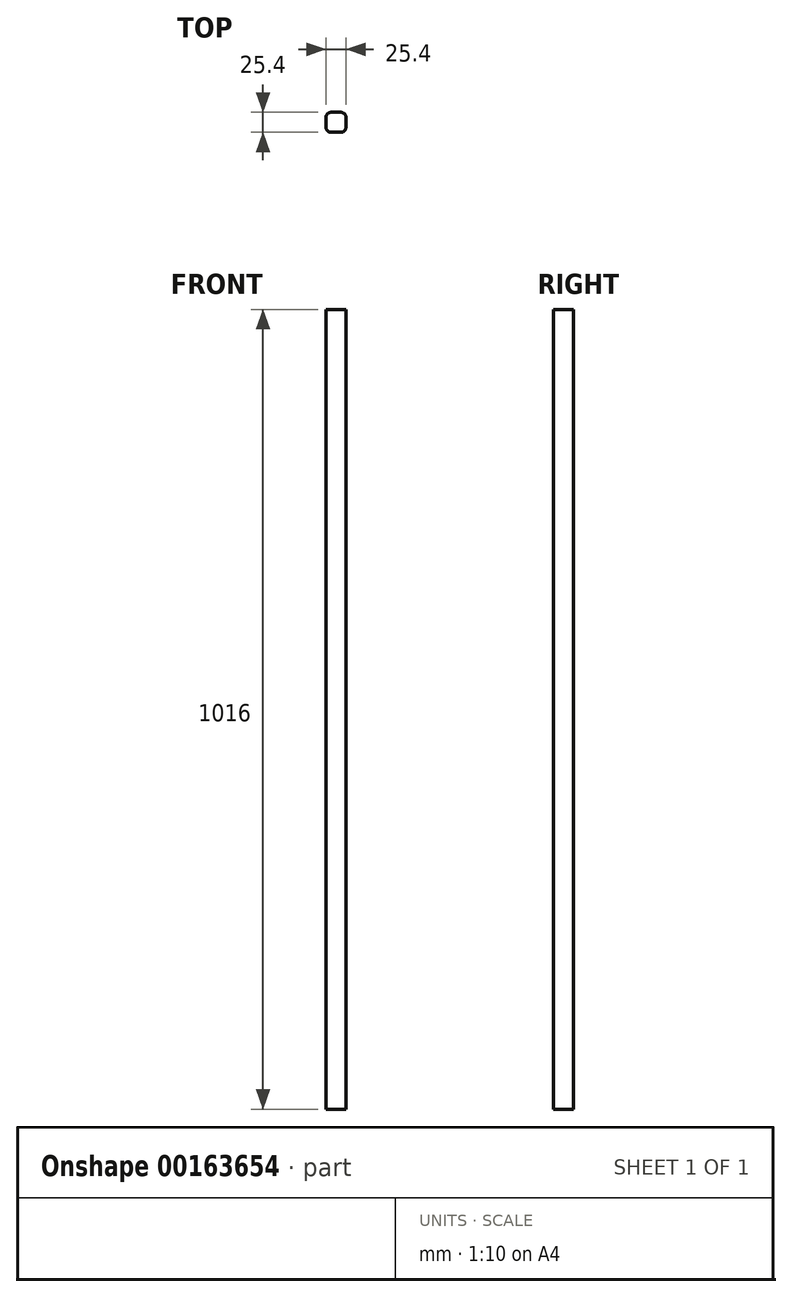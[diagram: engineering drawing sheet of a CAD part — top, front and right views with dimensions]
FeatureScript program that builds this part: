
annotation { "Feature Type Name" : "Feature", "Feature Type Description" : "" }
export const myFeature = defineFeature(function(context is Context, id is Id, definition is map)
    precondition{}
    {
        {
            var Q0;
            Q0=qCreatedBy(makeId("Top.planeOp"),FACE);
            var sketch = newSketch(context, id + "F0", { "sketchPlane" : qUnion([Q0])});
            skLineSegment(sketch, "E0.bottom", {"start": v(6.35, 12.7) * mm, "end": v(-6.35, 12.7) * mm});
            skLineSegment(sketch, "E0.top", {"start": v(6.35, -12.7) * mm, "end": v(-6.35, -12.7) * mm});
            skLineSegment(sketch, "E0.left", {"start": v(12.7, 6.35) * mm, "end": v(12.7, -6.35) * mm});
            skLineSegment(sketch, "E0.right", {"start": v(-12.7, 6.35) * mm, "end": v(-12.7, -6.35) * mm});
            skPoint(sketch, "E0.middle", {"position": v(0, 0) * mm});
            skPoint(sketch, "E1.visualSharp", {"position": v(-12.7, 12.7) * mm});
            skArc(sketch, "E1.filletArc", {"start": v(-6.35, 12.7) * mm, "mid": v(-10.84, 10.84) * mm, "end": v(-12.7, 6.35) * mm});
            skPoint(sketch, "E2.visualSharp", {"position": v(-12.7, -12.7) * mm});
            skArc(sketch, "E2.filletArc", {"start": v(-12.7, -6.35) * mm, "mid": v(-10.84, -10.84) * mm, "end": v(-6.35, -12.7) * mm});
            skPoint(sketch, "E3.visualSharp", {"position": v(12.7, -12.7) * mm});
            skArc(sketch, "E3.filletArc", {"start": v(6.35, -12.7) * mm, "mid": v(10.84, -10.84) * mm, "end": v(12.7, -6.35) * mm});
            skPoint(sketch, "E4.visualSharp", {"position": v(12.7, 12.7) * mm});
            skArc(sketch, "E4.filletArc", {"start": v(12.7, 6.35) * mm, "mid": v(10.84, 10.84) * mm, "end": v(6.35, 12.7) * mm});
            skSolve(sketch);
        }
        {
            var Q0;
            Q0=qSketchRegion(id+"F0",true);
            extrude(context, id + "F1", {"entities" : qUnion([Q0]), "depth" : 1016 * mm});
        }
    });
